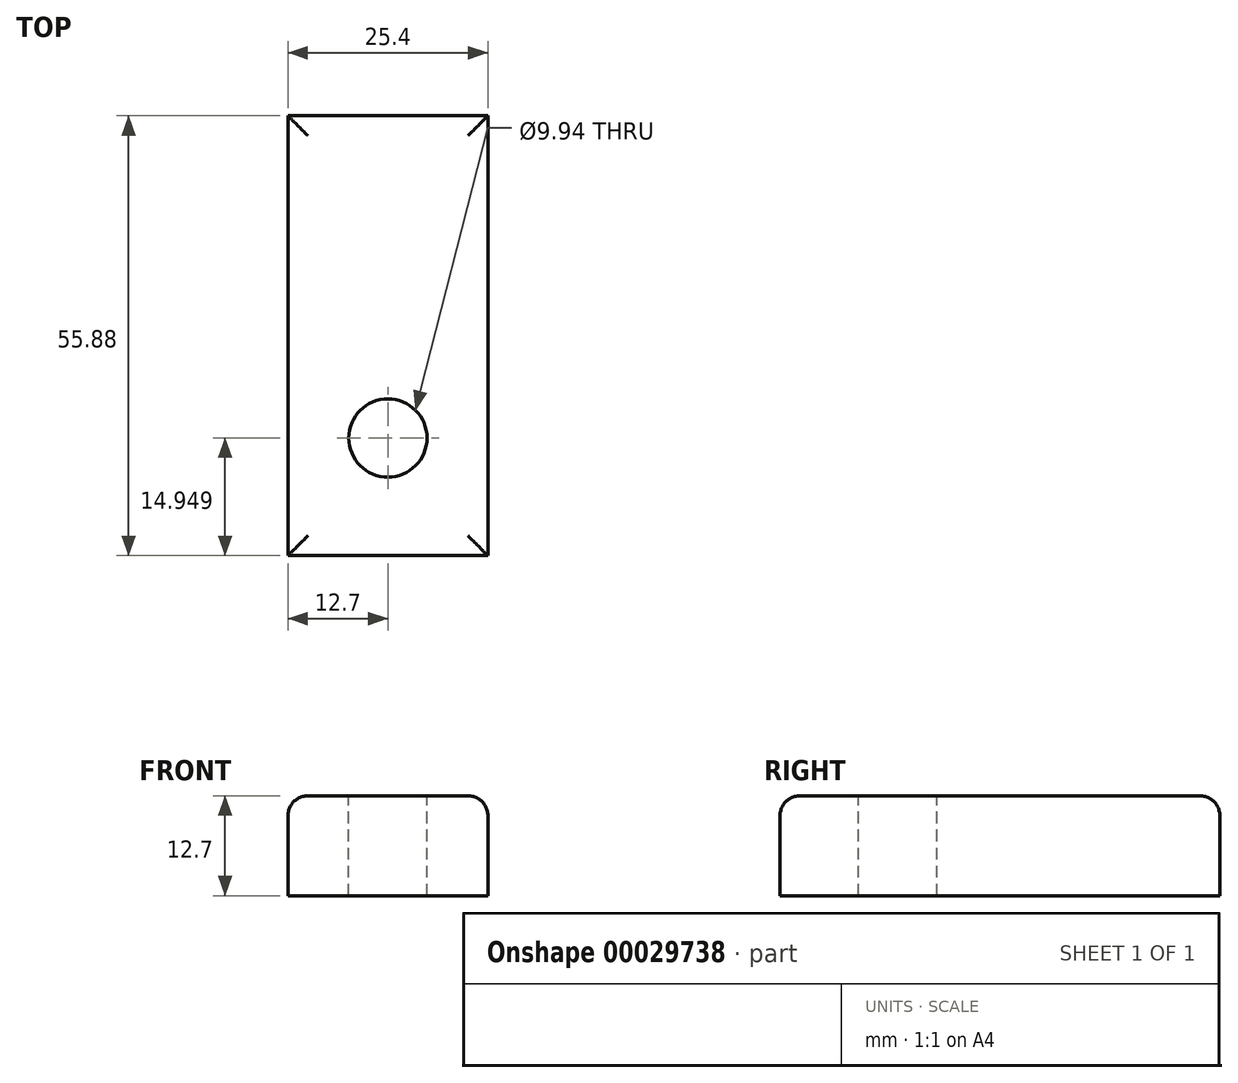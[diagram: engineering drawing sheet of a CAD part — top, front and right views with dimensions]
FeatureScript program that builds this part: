
annotation { "Feature Type Name" : "Feature", "Feature Type Description" : "" }
export const myFeature = defineFeature(function(context is Context, id is Id, definition is map)
    precondition{}
    {
        {
            var Q0;
            Q0=qCreatedBy(makeId("Top.planeOp"),FACE);
            var sketch = newSketch(context, id + "F0", { "sketchPlane" : qUnion([Q0])});
            skLineSegment(sketch, "E0.bottom", {"start": v(-12.7, 27.94) * mm, "end": v(12.7, 27.94) * mm});
            skLineSegment(sketch, "E0.top", {"start": v(-12.7, -27.94) * mm, "end": v(12.7, -27.94) * mm});
            skLineSegment(sketch, "E0.left", {"start": v(-12.7, 27.94) * mm, "end": v(-12.7, -27.94) * mm});
            skLineSegment(sketch, "E0.right", {"start": v(12.7, 27.94) * mm, "end": v(12.7, -27.94) * mm});
            skSolve(sketch);
        }
        {
            var Q0;
            Q0=makeQuery(id+"F0.imprint","IMPRINT",FACE,{"disambiguationData":[TD([[makeQuery(id+"F0.imprint","IMPRINT",EDGE,{"derivedFrom":sQuery(id+"F0.wireOp",EDGE,"E0.bottom")}),-1.0]])]});
            extrude(context, id + "F1", {"entities" : qUnion([Q0]), "depth" : 12.7 * mm});
        }
        {
            var Q0;
            Q0=makeQuery(id+"F1.opExtrude","CAP_EDGE",EDGE,{"disambiguationData":[OSD([sQuery(id+"F0.wireOp",EDGE,"E0.right")])],"isStart":false});
            var Q1;
            Q1=makeQuery(id+"F1.opExtrude","CAP_EDGE",EDGE,{"disambiguationData":[OSD([sQuery(id+"F0.wireOp",EDGE,"E0.left")])],"isStart":false});
            var Q2;
            Q2=makeQuery(id+"F1.opExtrude","CAP_EDGE",EDGE,{"disambiguationData":[OSD([sQuery(id+"F0.wireOp",EDGE,"E0.top")])],"isStart":false});
            var Q3;
            Q3=makeQuery(id+"F1.opExtrude","CAP_EDGE",EDGE,{"disambiguationData":[OSD([sQuery(id+"F0.wireOp",EDGE,"E0.bottom")])],"isStart":false});
            fillet(context, id + "F2", {"entities" : qUnion([Q0, Q1, Q2, Q3]), "radius" : 2.54 * mm, "tangentPropagation" : true, "allowEdgeOverflow" : false});
        }
        {
            var Q0;
            Q0=makeQuery(id+"F1.opExtrude","CAP_FACE",FACE,{"disambiguationData":[OSD([sQuery(id+"F0.wireOp",EDGE,"E0.bottom"),sQuery(id+"F0.wireOp",EDGE,"E0.top"),sQuery(id+"F0.wireOp",EDGE,"E0.left"),sQuery(id+"F0.wireOp",EDGE,"E0.right")])],"isStart":false});
            var sketch = newSketch(context, id + "F3", { "sketchPlane" : qUnion([Q0])});
            skCircle(sketch, "E1", {"center": v(0, -13) * mm, "radius": 4.97 * mm});
            skSolve(sketch);
        }
        {
            var Q0;
            Q0=makeQuery(id+"F3.imprint","IMPRINT",FACE,{"disambiguationData":[TD([[makeQuery(id+"F3.imprint","IMPRINT",EDGE,{"derivedFrom":sQuery(id+"F3.wireOp",EDGE,"E1")}),1.0]])]});
            var Q1;
            Q1=sQuery(id+"F3.wireOp",EDGE,"E1");
            extrude(context, id + "F4", {"entities" : qUnion([Q0]), "operationType" : NewBodyOperationType.REMOVE, "surfaceEntities" : qUnion([Q1]), "oppositeDirection" : true, "depth" : 25.4 * mm, "hasSecondDirection" : true, "secondDirectionOppositeDirection" : false, "secondDirectionDepth" : 25.4 * mm});
        }
    });
